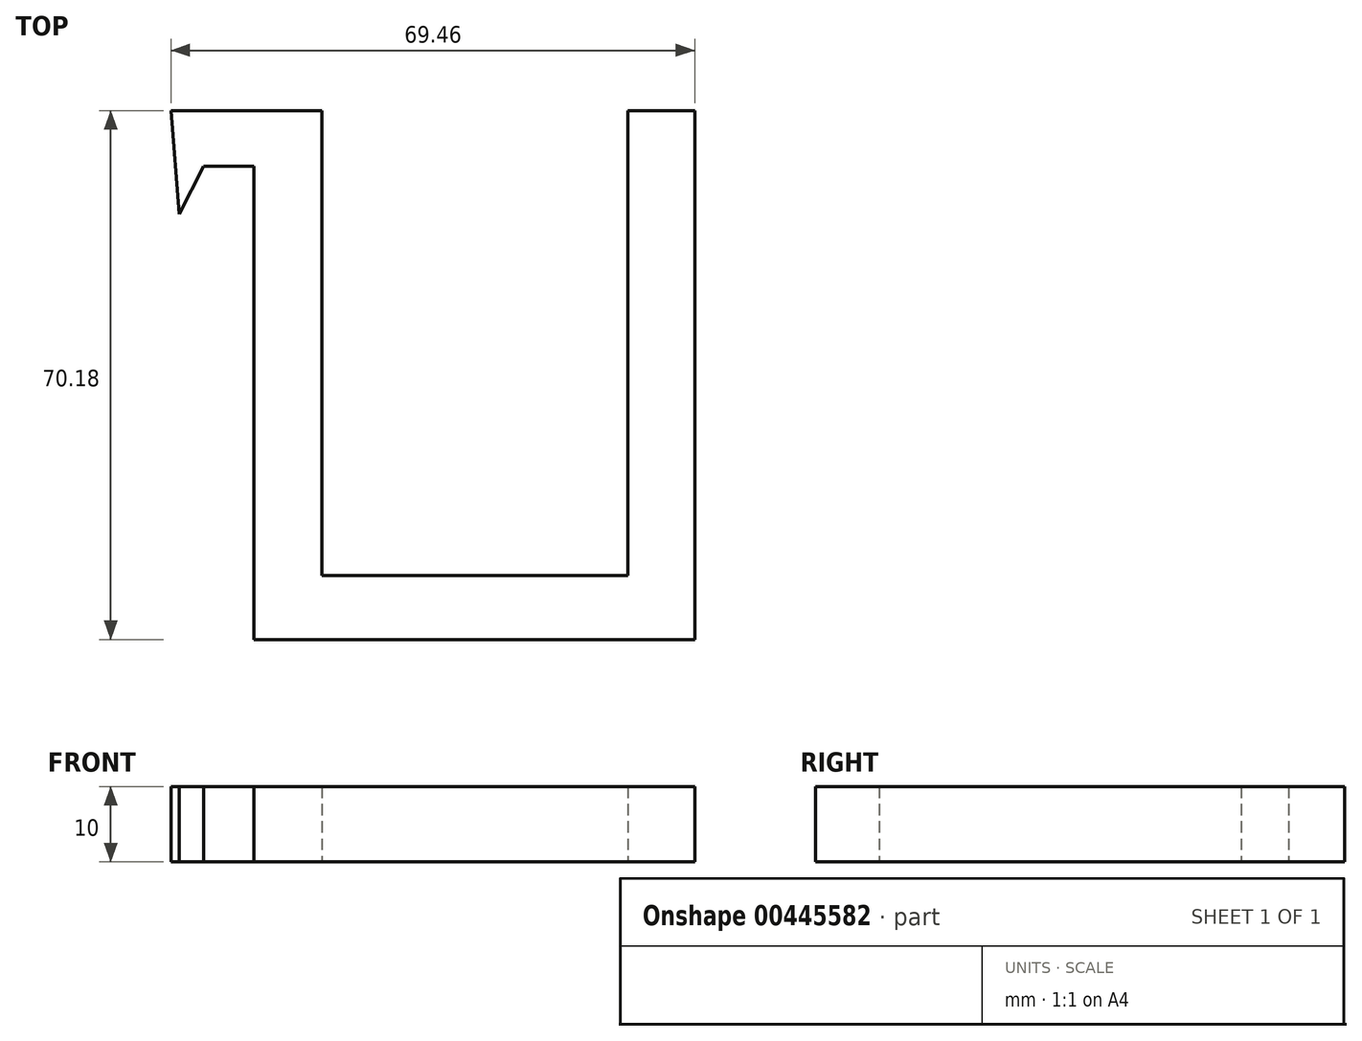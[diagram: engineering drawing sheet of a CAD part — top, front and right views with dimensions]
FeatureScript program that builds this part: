
annotation { "Feature Type Name" : "Feature", "Feature Type Description" : "" }
export const myFeature = defineFeature(function(context is Context, id is Id, definition is map)
    precondition{}
    {
        {
            var Q0;
            Q0=qCreatedBy(makeId("Top.planeOp"),FACE);
            var sketch = newSketch(context, id + "F0", { "sketchPlane" : qUnion([Q0])});
            skLineSegment(sketch, "E0", {"start": v(43.12, -14.16) * mm, "end": v(43.12, 56.02) * mm});
            skLineSegment(sketch, "E1", {"start": v(43.12, 56.02) * mm, "end": v(34.28, 56.02) * mm});
            skLineSegment(sketch, "E2", {"start": v(34.28, 56.02) * mm, "end": v(34.28, -5.68) * mm});
            skLineSegment(sketch, "E3", {"start": v(34.28, -5.68) * mm, "end": v(-6.31, -5.68) * mm});
            skLineSegment(sketch, "E4", {"start": v(-6.31, -5.68) * mm, "end": v(-6.31, 56.02) * mm});
            skLineSegment(sketch, "E5", {"start": v(-6.31, 56.02) * mm, "end": v(-15.15, 56.02) * mm});
            skLineSegment(sketch, "E6", {"start": v(-15.33, 48.62) * mm, "end": v(-15.33, -14.16) * mm});
            skLineSegment(sketch, "E7", {"start": v(-15.33, -14.16) * mm, "end": v(43.12, -14.16) * mm});
            skLineSegment(sketch, "E8", {"start": v(-15.15, 56.02) * mm, "end": v(-26.34, 56.02) * mm});
            skLineSegment(sketch, "E9", {"start": v(-26.34, 56.02) * mm, "end": v(-25.26, 42.3) * mm});
            skLineSegment(sketch, "E10", {"start": v(-25.26, 42.3) * mm, "end": v(-22, 48.62) * mm});
            skLineSegment(sketch, "E11", {"start": v(-22, 48.62) * mm, "end": v(-15.33, 48.62) * mm});
            skSolve(sketch);
        }
        {
            var Q0;
            Q0 = qSketchRegion(id + "F0", true);
            extrude(context, id + "F1", {"entities" : qUnion([Q0]), "depth" : 10 * mm});
        }
    });
